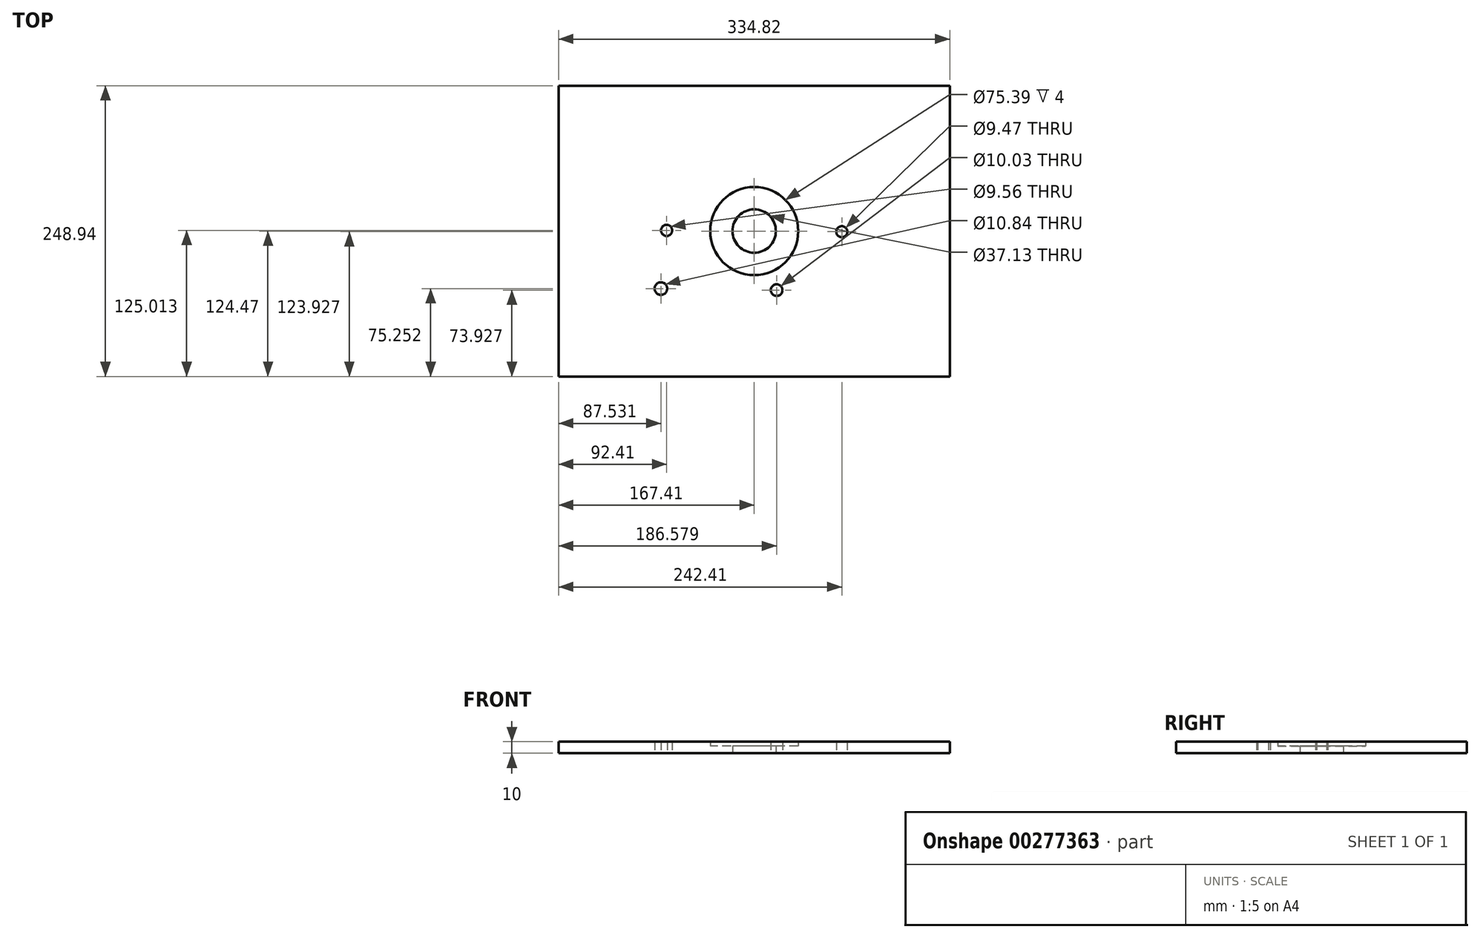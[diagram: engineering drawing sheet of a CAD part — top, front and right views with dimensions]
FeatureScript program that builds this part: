
annotation { "Feature Type Name" : "Feature", "Feature Type Description" : "" }
export const myFeature = defineFeature(function(context is Context, id is Id, definition is map)
    precondition{}
    {
        {
            var Q0;
            Q0=qCreatedBy(makeId("Top.planeOp"),FACE);
            var sketch = newSketch(context, id + "F0", { "sketchPlane" : qUnion([Q0])});
            skLineSegment(sketch, "E0.bottom", {"start": v(167.4, -124.47) * mm, "end": v(-167.4, -124.47) * mm});
            skLineSegment(sketch, "E0.top", {"start": v(167.4, 124.47) * mm, "end": v(-167.4, 124.47) * mm});
            skLineSegment(sketch, "E0.left", {"start": v(167.4, -124.47) * mm, "end": v(167.4, 124.47) * mm});
            skLineSegment(sketch, "E0.right", {"start": v(-167.4, -124.47) * mm, "end": v(-167.4, 124.47) * mm});
            skPoint(sketch, "E0.middle", {"position": v(0, 0) * mm});
            skCircle(sketch, "E1", {"center": v(0, 0) * mm, "radius": 18.56 * mm});
            skCircle(sketch, "E2", {"center": v(0, 0) * mm, "radius": 37.7 * mm});
            skCircle(sketch, "E3", {"center": v(75, -0.54) * mm, "radius": 4.74 * mm});
            skCircle(sketch, "E4", {"center": v(19.17, -50.54) * mm, "radius": 5.02 * mm});
            skCircle(sketch, "E5", {"center": v(-75, 0.54) * mm, "radius": 4.78 * mm});
            skCircle(sketch, "E6", {"center": v(-79.88, -49.22) * mm, "radius": 5.42 * mm});
            skSolve(sketch);
        }
        {
            var Q0;
            Q0=makeQuery(id+"F0.imprint","IMPRINT",FACE,{"disambiguationData":[TD([[makeQuery(id+"F0.imprint","IMPRINT",EDGE,{"derivedFrom":sQuery(id+"F0.wireOp",EDGE,"E0.bottom")}),-1.0]])]});
            extrude(context, id + "F1", {"entities" : qUnion([Q0]), "depth" : 10 * mm});
        }
        {
            var Q0;
            Q0=makeQuery(id+"F0.imprint","IMPRINT",FACE,{"disambiguationData":[TD([[makeQuery(id+"F0.imprint","IMPRINT",EDGE,{"derivedFrom":sQuery(id+"F0.wireOp",EDGE,"E1")}),-1.0]])]});
            extrude(context, id + "F2", {"entities" : qUnion([Q0]), "operationType" : NewBodyOperationType.ADD, "depth" : 6 * mm});
        }
    });
